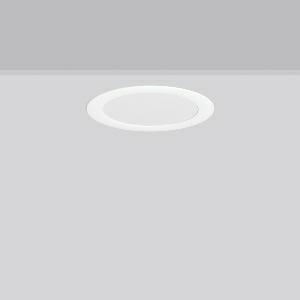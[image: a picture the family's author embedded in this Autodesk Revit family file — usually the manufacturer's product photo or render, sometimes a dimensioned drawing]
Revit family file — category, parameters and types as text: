
# Revit family: toledo_flat_round_e_901715_002_19_d0ba
name_source: partatom
category: Lighting Fixtures
units: mm (PartAtom-declared; Revit-internal decimal feet)

## family parameters
Cut with Voids When Loaded = No
Host = Face
Light Source = No
Part Type = Normal
Room Calculation Point = No
Round Connector Dimension = Use Diameter
Shared = No

## types (1)
- TOLEDO FLAT round E (1 x LED Modul 830, 1650 lm, 3000)
    Apparent Load = 17 VA
    CIE Flux Codes = 48 79 96 100 100
    Color Rendering = 80
    Color Temperature = 3000
    Default Elevation = 1800 mm
    Description = Series: TOLEDO FLAT round
Ultra thin recessed downlight. Housing: die-cast aluminium. Light guide and diffuser made of non-yellowing PMMA, opal matt. Ceiling installation with spring system. Mounting depth depends on ceiling strength. Including separate LED converter with connecting cable 250 mm.Connected HF motion detector in a separate ballast box. Adjustable dim functions Soft Start, Corridor, Permanent. Wireless networking, sensor configuration and communication via Bluetooth. Operation via an Android / iOS device, free app available for download. master/slave Brightness sensor without function. Not suitable for metal ceilings.Versions with movement sensor not suitable for surface-mounted housing. Suitable for through-wiring with separately available accessories. Retrofittable decorative cylinders made of chintz fabric as accessory, optional with satin finish plastic diffuser. Through-wiring box (5 pole) available as accessory. 
Colour: white
Diameter: 255 mm
Height: 3 mm
Cut-out diameter: 234 mm
Recess height: 55-76 mm
Luminaire: recess height: 31-51 mm
Lamp: LED
Socket: without socket
Colour temperature: 3000K
Colour rendering index (CRI): 80
System power: 17 W
Rated luminous flux: 1650 lm
Luminous efficiency: 97 lm/W
Control gear: Dimmable Bluetooth converter
Protection class: I
Type of protection: IP 54
    Height = 0 mm  [stored 0 ft]
    Lamp = 1 x LED Modul 830
    Lamp Light Flux = 1650 lm
    Lamp count = 1
    Length = 255 mm
    Lifetime = 50000 h
    Luminous efficacy = 97 lm/W
    Manufacturer = RZB
    ModVariant = No
    Model = 901715.002.19
    Mounting Place = Ceiling
    Mounting Type = Recessed
    Number of Poles = 1
    OnlyDefault = Yes
    Power Factor = 1
    Product Name = TOLEDO FLAT round E
    Product group = Recessed downlights
    ProductGroupID = 402
    Protection Class = Protection class I
    Protection Degree = IP 20
    RLX_Detail_Level = 1
    RLX_Emergency_Light_Flux = 0 lm
    RLX_Emergency_Type = 0
    RLX_Emergency_Type_DB = No
    RlxData = <blob elided: 30173 chars, md5=fc395358>
    Socket = socket
    Standby Power = 0 W
    System Light Flux = 1650 lm
    System Power = 17 W
    Type Comments = Product without accessories
    Type Image = 901453.002.jpg
    URL = http://relux.com
    VarID = ---
    Voltage = 230 V
    Voltage Range = 220-240 V
    Weight = 0.00 kg
    Width = 0 mm  [stored 0 ft]

note: [stored X ft] marks values corroborated as IEEE doubles in the binary element streams (Revit-internal decimal feet)

## geometry (parser evidence)
native form markers: Blend x4, Sweep x11
no freeform markers — native parametric forms only
